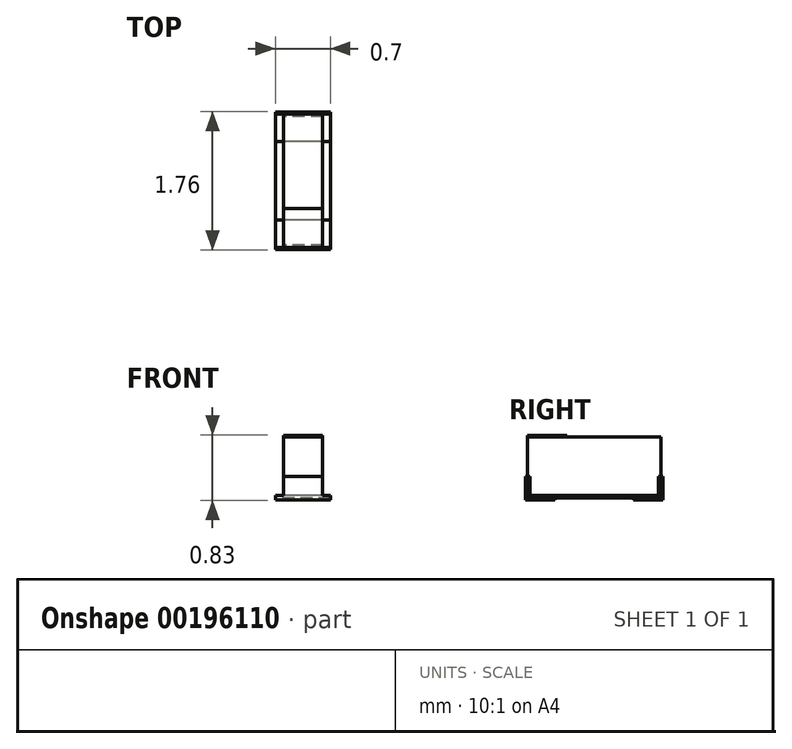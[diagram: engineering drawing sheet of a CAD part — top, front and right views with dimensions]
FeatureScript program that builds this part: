
annotation { "Feature Type Name" : "Feature", "Feature Type Description" : "" }
export const myFeature = defineFeature(function(context is Context, id is Id, definition is map)
    precondition{}
    {
        {
            var Q0;
            Q0=qCreatedBy(makeId("Top.planeOp"),FACE);
            var sketch = newSketch(context, id + "F0", { "sketchPlane" : qUnion([Q0])});
            skLineSegment(sketch, "E0.bottom", {"start": v(0.45, -0.85) * mm, "end": v(-0.45, -0.85) * mm});
            skLineSegment(sketch, "E0.top", {"start": v(0.45, 0.85) * mm, "end": v(-0.45, 0.85) * mm});
            skLineSegment(sketch, "E0.left", {"start": v(0.45, -0.85) * mm, "end": v(0.45, 0.85) * mm});
            skLineSegment(sketch, "E0.right", {"start": v(-0.45, -0.85) * mm, "end": v(-0.45, 0.85) * mm});
            skPoint(sketch, "E0.middle", {"position": v(0, 0) * mm});
            skSolve(sketch);
        }
        {
            var Q0;
            Q0 = qSketchRegion(id + "F0", true);
            extrude(context, id + "F1", {"entities" : qUnion([Q0]), "depth" : 0.78 * mm});
        }
        {
            var Q0;
            Q0=makeQuery(id+"F1.opExtrude","CAP_FACE",FACE,{"disambiguationData":[OSD([sQuery(id+"F0.wireOp",EDGE,"E0.bottom"),sQuery(id+"F0.wireOp",EDGE,"E0.top"),sQuery(id+"F0.wireOp",EDGE,"E0.left"),sQuery(id+"F0.wireOp",EDGE,"E0.right")])],"isStart":false});
            var sketch = newSketch(context, id + "F2", { "sketchPlane" : qUnion([Q0])});
            skLineSegment(sketch, "E1.bottom", {"start": v(-0.45, -0.85) * mm, "end": v(0.45, -0.85) * mm});
            skLineSegment(sketch, "E1.top", {"start": v(-0.45, -0.35) * mm, "end": v(0.45, -0.35) * mm});
            skLineSegment(sketch, "E1.left", {"start": v(-0.45, -0.85) * mm, "end": v(-0.45, -0.35) * mm});
            skLineSegment(sketch, "E1.right", {"start": v(0.45, -0.85) * mm, "end": v(0.45, -0.35) * mm});
            skSolve(sketch);
        }
        {
            var Q0;
            Q0 = qSketchRegion(id + "F2", true);
            extrude(context, id + "F3", {"entities" : qUnion([Q0]), "depth" : 0.02 * mm});
        }
        {
            var Q0;
            Q0=qCreatedBy(makeId("Right.planeOp"),FACE);
            var sketch = newSketch(context, id + "F4", { "sketchPlane" : qUnion([Q0])});
            skLineSegment(sketch, "E2", {"start": v(-0.81, 0.27) * mm, "end": v(-0.88, 0.27) * mm});
            skLineSegment(sketch, "E3", {"start": v(-0.88, 0.27) * mm, "end": v(-0.88, -0.02) * mm});
            skLineSegment(sketch, "E4", {"start": v(-0.88, -0.03) * mm, "end": v(-0.5, -0.02) * mm});
            skLineSegment(sketch, "E5", {"start": v(-0.5, -0.02) * mm, "end": v(-0.5, 0.04) * mm});
            skLineSegment(sketch, "E6", {"start": v(-0.5, 0.04) * mm, "end": v(-0.81, 0.03) * mm});
            skLineSegment(sketch, "E7", {"start": v(-0.81, 0.03) * mm, "end": v(-0.81, 0.27) * mm});
            skLineSegment(sketch, "E8", {"start": v(0, 0) * mm, "end": v(0, 0.78) * mm, "construction": true});
            skLineSegment(sketch, "E9.MirrorCS", {"start": v(0.81, 0.27) * mm, "end": v(0.88, 0.27) * mm});
            skLineSegment(sketch, "E10.MirrorCS", {"start": v(0.88, 0.27) * mm, "end": v(0.88, -0.02) * mm});
            skLineSegment(sketch, "E11.MirrorCS", {"start": v(0.88, -0.03) * mm, "end": v(0.5, -0.02) * mm});
            skLineSegment(sketch, "E12.MirrorCS", {"start": v(0.81, 0.03) * mm, "end": v(0.81, 0.27) * mm});
            skLineSegment(sketch, "E13.MirrorCS", {"start": v(0.5, 0.04) * mm, "end": v(0.81, 0.04) * mm});
            skLineSegment(sketch, "E14.MirrorCS", {"start": v(0.5, -0.02) * mm, "end": v(0.5, 0.04) * mm});
            skSolve(sketch);
        }
        {
            var Q0;
            Q0 = qSketchRegion(id + "F4", true);
            extrude(context, id + "F5", {"entities" : qUnion([Q0]), "endBound" : BoundingType.SYMMETRIC, "depth" : 0.92 * mm});
        }
        {
            var Q0;
            Q0=qCreatedBy(makeId("Front.planeOp"),FACE);
            var sketch = newSketch(context, id + "F6", { "sketchPlane" : qUnion([Q0])});
            skLineSegment(sketch, "E15", {"start": v(-0.58, 0.8) * mm, "end": v(-0.58, -0.03) * mm});
            skLineSegment(sketch, "E16", {"start": v(-0.58, -0.03) * mm, "end": v(-0.35, -0.03) * mm});
            skLineSegment(sketch, "E17", {"start": v(-0.35, -0.03) * mm, "end": v(-0.35, 0.03) * mm});
            skLineSegment(sketch, "E18", {"start": v(-0.35, 0.03) * mm, "end": v(-0.25, 0.03) * mm});
            skLineSegment(sketch, "E19", {"start": v(-0.25, 0.03) * mm, "end": v(-0.25, 0.8) * mm});
            skLineSegment(sketch, "E20", {"start": v(-0.25, 0.8) * mm, "end": v(-0.58, 0.8) * mm});
            skLineSegment(sketch, "E21", {"start": v(0, -0.03) * mm, "end": v(0, 0.8) * mm, "construction": true});
            skLineSegment(sketch, "E22.MirrorCS", {"start": v(0.58, 0.8) * mm, "end": v(0.58, -0.03) * mm});
            skLineSegment(sketch, "E23.MirrorCS", {"start": v(0.35, -0.03) * mm, "end": v(0.35, 0.03) * mm});
            skLineSegment(sketch, "E24.MirrorCS", {"start": v(0.58, -0.03) * mm, "end": v(0.35, -0.03) * mm});
            skLineSegment(sketch, "E25.MirrorCS", {"start": v(0.25, 0.8) * mm, "end": v(0.58, 0.8) * mm});
            skLineSegment(sketch, "E26.MirrorCS", {"start": v(0.35, 0.03) * mm, "end": v(0.25, 0.03) * mm});
            skLineSegment(sketch, "E27.MirrorCS", {"start": v(0.25, 0.03) * mm, "end": v(0.25, 0.8) * mm});
            skSolve(sketch);
        }
        {
            var Q0;
            Q0 = qSketchRegion(id + "F6", true);
            extrude(context, id + "F7", {"entities" : qUnion([Q0]), "operationType" : NewBodyOperationType.REMOVE, "endBound" : BoundingType.THROUGH_ALL, "oppositeDirection" : true, "depth" : 25 * mm, "hasSecondDirection" : true, "secondDirectionBound" : SecondDirectionBoundingType.THROUGH_ALL, "secondDirectionOppositeDirection" : false, "secondDirectionDepth" : 25 * mm});
        }
    });
